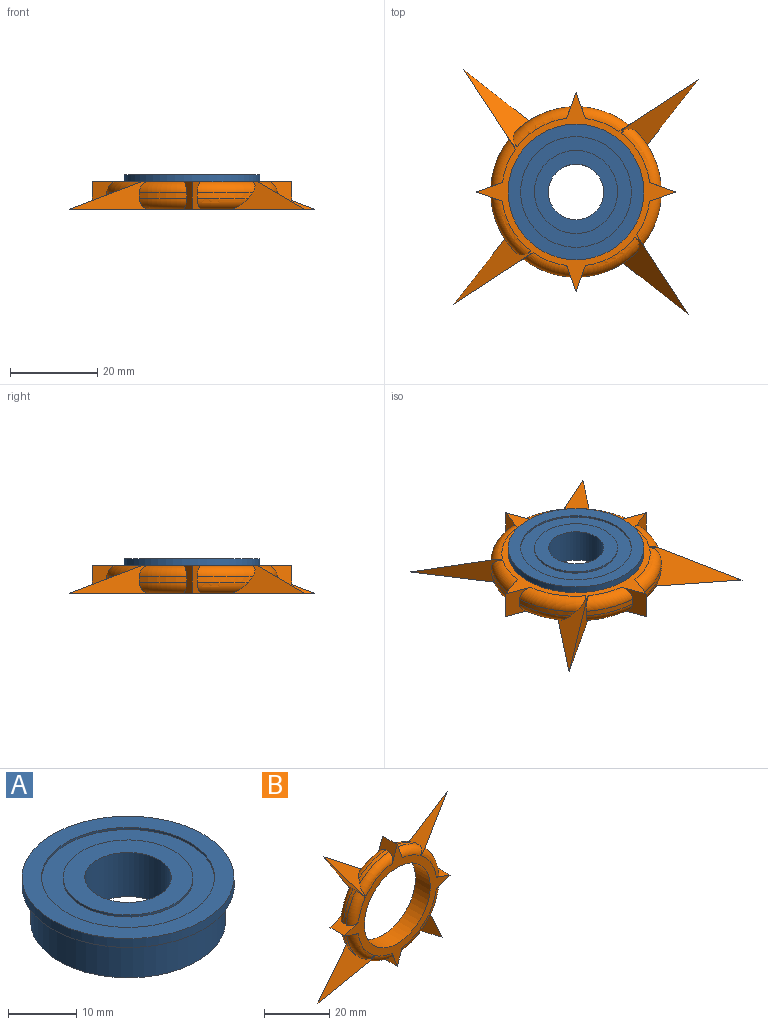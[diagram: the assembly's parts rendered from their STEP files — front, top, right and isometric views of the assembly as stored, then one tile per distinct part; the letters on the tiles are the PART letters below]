
ASSEMBLY  parts=2 mates=1
PART A: 10 faces, bbox 31.1x31.1x7.9 mm
  f0: cylinder r=12.7mm len=25.4mm, axis (0,0,1), area 30.4mm2, adj f8,f9
  f1: cylinder r=15.56mm len=31.12mm, axis (0,0,1), area 155.2mm2, adj f7,f8
  f2: cylinder r=14.29mm len=28.58mm, axis (0,0,1), area 570mm2, adj f6,f7
  f3: cylinder r=6.35mm len=12.7mm, axis (0,0,1), area 316.7mm2, adj f5,f6
  f4: cylinder r=9.53mm len=19.05mm, axis (0,0,1), area 22.8mm2, adj f5,f9
  f5: plane 19.05x19.05mm, normal (0,0,1), area 158.3mm2, adj f3,f4
  f6: plane 28.58x28.58mm, normal (0,0,-1), area 514.6mm2, adj f2,f3
  f7: plane 31.12x31.12mm, normal (0,0,-1), area 119.1mm2, adj f1,f2
  f8: plane 31.12x31.12mm, normal (0,0,1), area 253.7mm2, adj f0,f1
  f9: plane 25.4x25.4mm, normal (0,0,1), area 221.7mm2, adj f0,f4
PART B: 43 faces, bbox 56.1x6.4x56.1 mm
  f0: plane 6.35x5.99mm, normal (0.94,0,-0.34), area 25.6mm2, adj f1,f19,f21,f22,f29,f37
  f1: cylinder r=19.55mm len=12.61mm, axis (0,1,0), area 17.1mm2, adj f0,f29,f37,f41
  f2: plane 18.19x11.92mm, normal (0.84,0,0.55), area 61.2mm2, adj f3,f21,f22,f28,f36,f41
  f3: cylinder r=19.55mm len=10.9mm, axis (0,1,0), area 15.1mm2, adj f2,f4,f28,f36
  f4: plane 6.35x5.99mm, normal (0.34,0,-0.94), area 25.6mm2, adj f3,f5,f21,f22,f28,f36
  f5: plane 6.35x5.99mm, normal (0.34,0,0.94), area 25.6mm2, adj f4,f6,f21,f22,f27,f35
  f6: cylinder r=19.55mm len=12.61mm, axis (0,1,0), area 17.1mm2, adj f5,f27,f35,f42
  f7: plane 18.19x11.92mm, normal (-0.55,0,0.84), area 61.2mm2, adj f8,f21,f22,f26,f34,f42
  f8: cylinder r=19.55mm len=10.9mm, axis (0,1,0), area 15.1mm2, adj f7,f9,f26,f34
  f9: plane 6.35x5.99mm, normal (0.94,0,0.34), area 25.6mm2, adj f8,f10,f21,f22,f26,f34
  f10: plane 6.35x5.99mm, normal (-0.94,0,0.34), area 25.6mm2, adj f9,f11,f21,f22,f25,f33
  f11: cylinder r=19.55mm len=12.61mm, axis (0,1,0), area 17.1mm2, adj f10,f25,f33,f39
  f12: plane 18.19x11.92mm, normal (-0.84,0,-0.55), area 61.2mm2, adj f13,f21,f22,f24,f32,f39
  f13: cylinder r=19.55mm len=10.9mm, axis (0,1,0), area 15.1mm2, adj f12,f14,f24,f32
  f14: plane 6.35x5.99mm, normal (-0.34,0,0.94), area 25.6mm2, adj f13,f15,f21,f22,f24,f32
  f15: plane 6.35x5.99mm, normal (-0.34,0,-0.94), area 25.6mm2, adj f14,f16,f21,f22,f23,f31
  f16: cylinder r=19.55mm len=12.61mm, axis (0,1,0), area 17.1mm2, adj f15,f23,f31,f40
  f17: plane 18.19x11.92mm, normal (0.55,0,-0.84), area 61.2mm2, adj f18,f21,f22,f30,f38,f40
  f18: cylinder r=19.55mm len=10.9mm, axis (0,1,0), area 15.1mm2, adj f17,f19,f30,f38
  f19: plane 6.35x5.99mm, normal (-0.94,0,-0.34), area 25.6mm2, adj f0,f18,f21,f22,f30,f38
  f20: cylinder r=14.29mm len=28.58mm, axis (0,1,0), area 570mm2, adj f21,f22
  f21: plane 45.72x45.72mm, normal (0,-1,0), area 320.4mm2, adj f0,f2,f4,f5,f7,f9,f10,f12
  f22: plane 56.08x56.08mm, normal (0,1,0), area 615mm2, adj f0,f2,f4,f5,f7,f9,f10,f12
  f23: torus R=17.01mm, axis (0,-1,0), area 39.8mm2, adj f15,f16,f22,f40
  f24: torus R=17.01mm, axis (0,-1,0), area 42.2mm2, adj f12,f13,f14,f22
  f25: torus R=17.01mm, axis (0,-1,0), area 39.8mm2, adj f10,f11,f22,f39
  f26: torus R=17.01mm, axis (0,-1,0), area 42.2mm2, adj f7,f8,f9,f22
  f27: torus R=17.01mm, axis (0,-1,0), area 39.8mm2, adj f5,f6,f22,f42
  f28: torus R=17.01mm, axis (0,-1,0), area 42.2mm2, adj f2,f3,f4,f22
  f29: torus R=17.01mm, axis (0,-1,0), area 39.8mm2, adj f0,f1,f22,f41
  f30: torus R=17.01mm, axis (0,-1,0), area 42.2mm2, adj f17,f18,f19,f22
  f31: torus R=17.01mm, axis (0,-1,0), area 58.1mm2, adj f15,f16,f21,f40
  f32: torus R=17.01mm, axis (0,-1,0), area 42.2mm2, adj f12,f13,f14,f21
  f33: torus R=17.01mm, axis (0,-1,0), area 58.1mm2, adj f10,f11,f21,f39
  f34: torus R=17.01mm, axis (0,-1,0), area 42.2mm2, adj f7,f8,f9,f21
  f35: torus R=17.01mm, axis (0,-1,0), area 58.1mm2, adj f5,f6,f21,f42
  f36: torus R=17.01mm, axis (0,-1,0), area 42.2mm2, adj f2,f3,f4,f21
  f37: torus R=17.01mm, axis (0,-1,0), area 58.1mm2, adj f0,f1,f21,f41
  f38: torus R=17.01mm, axis (0,-1,0), area 42.2mm2, adj f17,f18,f19,f21
  f39: plane 17.68x17.14mm, normal (0.44,-0.71,0.56), area 84.9mm2, adj f11,f12,f21,f22,f25,f33
  f40: plane 17.68x17.14mm, normal (-0.56,-0.71,0.44), area 84.9mm2, adj f16,f17,f21,f22,f23,f31
  f41: plane 17.68x17.14mm, normal (-0.44,-0.71,-0.56), area 84.9mm2, adj f1,f2,f21,f22,f29,f37
  f42: plane 17.68x17.14mm, normal (0.56,-0.71,-0.44), area 84.9mm2, adj f6,f7,f21,f22,f27,f35
PLACE A t=(34.45,28.39,8.78)mm
PLACE B rot(axis=(-1,0,0),90deg) t=(34.45,28.39,8.78)mm
MATE fastened B.f20 <-> A.f0  axis (0,0,1) through (34.45,28.39,15.13)mm
